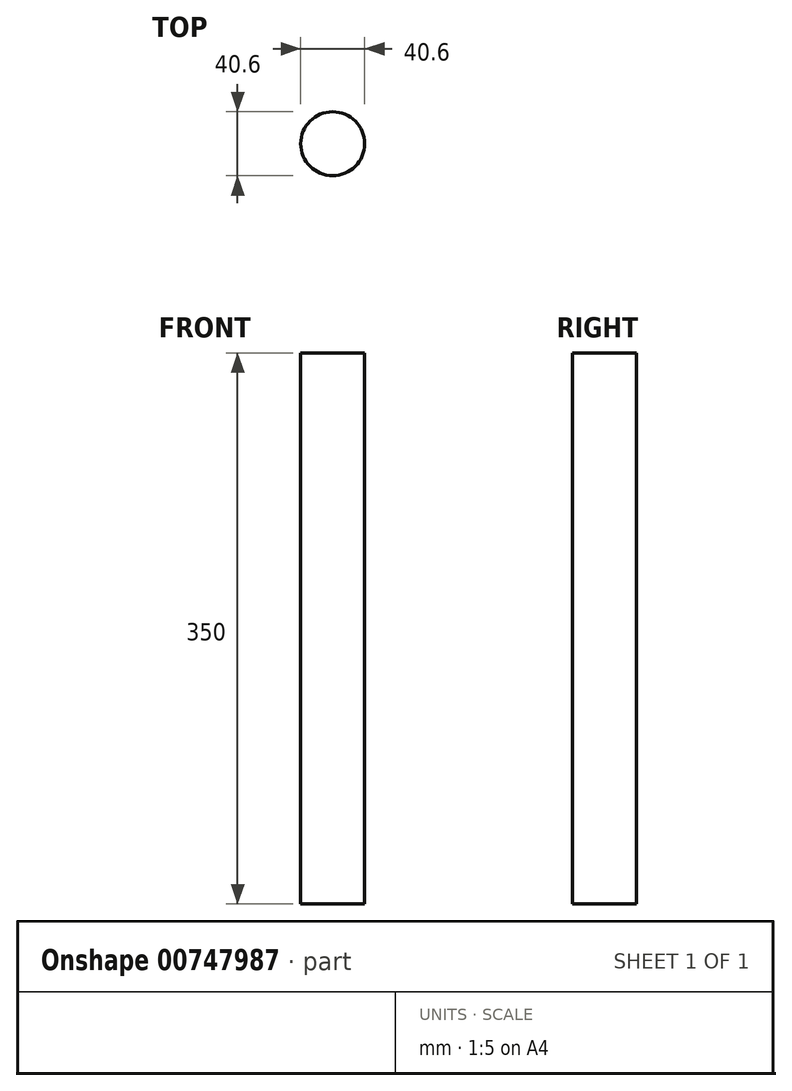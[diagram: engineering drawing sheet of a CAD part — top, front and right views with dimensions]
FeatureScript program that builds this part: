
annotation { "Feature Type Name" : "Feature", "Feature Type Description" : "" }
export const myFeature = defineFeature(function(context is Context, id is Id, definition is map)
    precondition{}
    {
        {
            var Q0;
            Q0=qCreatedBy(makeId("Top.planeOp"),FACE);
            var sketch = newSketch(context, id + "F0", { "sketchPlane" : qUnion([Q0])});
            skCircle(sketch, "E0", {"center": v(0, 0) * mm, "radius": 20.3 * mm});
            skSolve(sketch);
        }
        {
            var Q0;
            Q0=makeQuery(id+"F0.imprint","IMPRINT",FACE,{"disambiguationData":[TD([[makeQuery(id+"F0.imprint","IMPRINT",EDGE,{"derivedFrom":sQuery(id+"F0.wireOp",EDGE,"E0")}),1.0]])]});
            extrude(context, id + "F1", {"entities" : qUnion([Q0]), "endBound" : BoundingType.SYMMETRIC, "depth" : 350 * mm, "offsetDistance" : 25 * mm});
        }
    });
